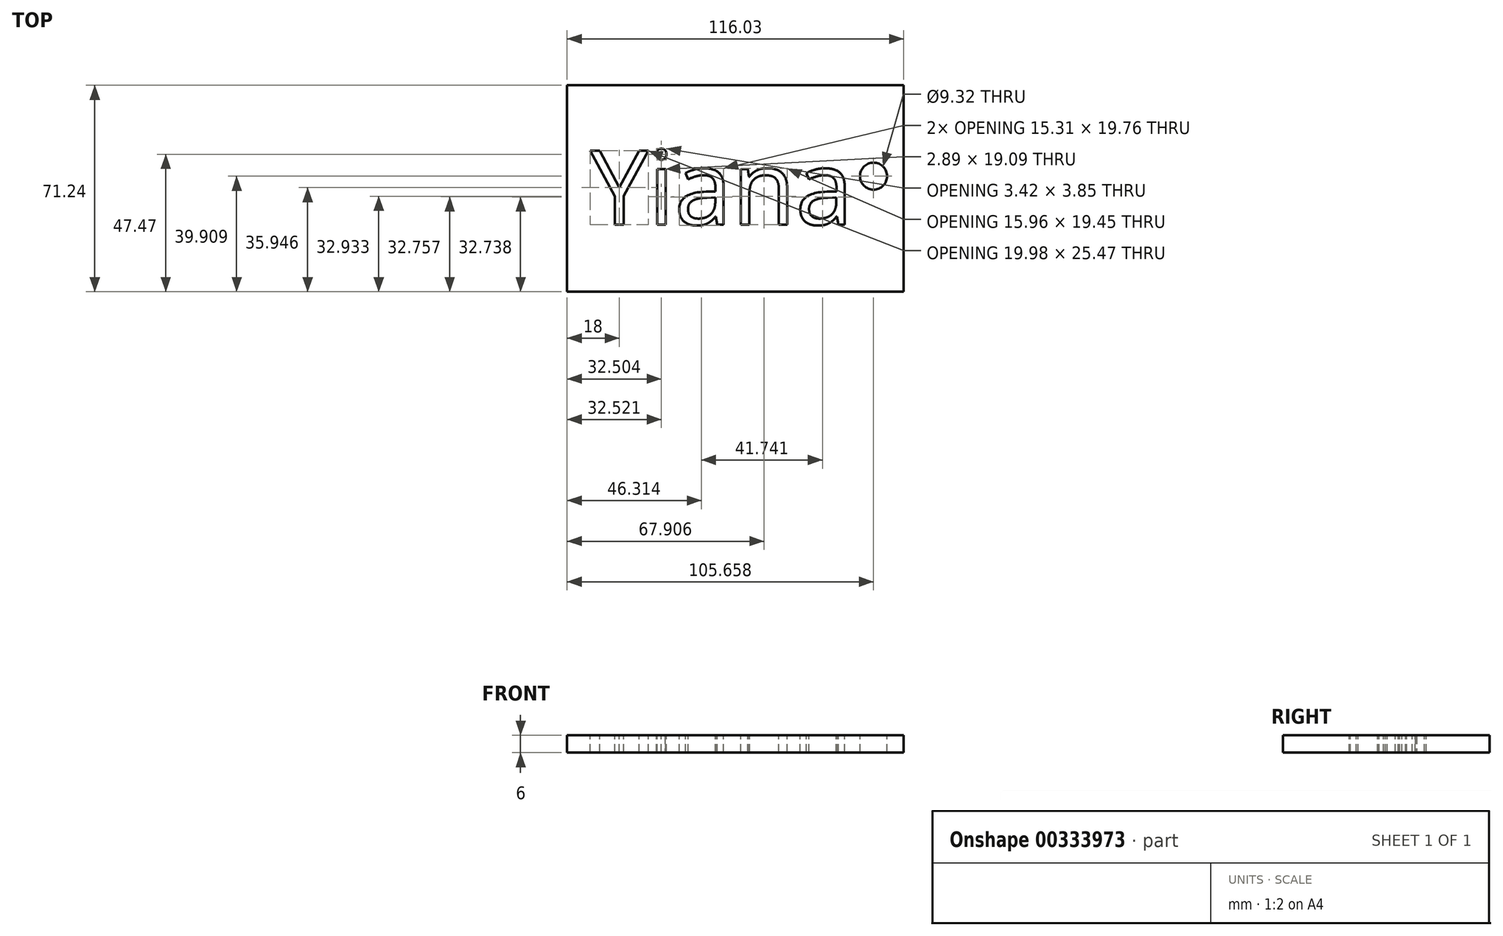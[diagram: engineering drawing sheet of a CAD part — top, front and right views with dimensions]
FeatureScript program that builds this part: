
annotation { "Feature Type Name" : "Feature", "Feature Type Description" : "" }
export const myFeature = defineFeature(function(context is Context, id is Id, definition is map)
    precondition{}
    {
        {
            var Q0;
            Q0=qCreatedBy(makeId("Top.planeOp"),FACE);
            var sketch = newSketch(context, id + "F0", { "sketchPlane" : qUnion([Q0])});
            skLineSegment(sketch, "E0.bottom", {"start": v(-77.55, 35.92) * mm, "end": v(38.48, 35.92) * mm});
            skLineSegment(sketch, "E0.top", {"start": v(-77.55, -35.32) * mm, "end": v(38.48, -35.32) * mm});
            skLineSegment(sketch, "E0.left", {"start": v(-77.55, 35.92) * mm, "end": v(-77.55, -35.32) * mm});
            skLineSegment(sketch, "E0.right", {"start": v(38.48, 35.92) * mm, "end": v(38.48, -35.32) * mm});
            skSolve(sketch);
        }
        {
            var Q0;
            Q0 = qSketchRegion(id + "F0", true);
            extrude(context, id + "F1", {"entities" : qUnion([Q0]), "depth" : 6 * mm});
        }
        {
            var Q0;
            Q0=makeQuery(id+"F1.opExtrude","CAP_FACE",FACE,{"disambiguationData":[OSD([sQuery(id+"F0.wireOp",EDGE,"E0.bottom"),sQuery(id+"F0.wireOp",EDGE,"E0.top"),sQuery(id+"F0.wireOp",EDGE,"E0.left"),sQuery(id+"F0.wireOp",EDGE,"E0.right")])],"isStart":false});
            var sketch = newSketch(context, id + "F2", { "sketchPlane" : qUnion([Q0])});
            skText(sketch, "E1", { "text": "Yiana\n", "fontName": "OpenSans-Regular.ttf"});
            skCircle(sketch, "E2", {"center": v(28.1, 4.59) * mm, "radius": 4.66 * mm});
            const initialGuessF2  = {"E1": [-0.06954, -0.01211, 1, 0, 0.02569]};
            skSetInitialGuess(sketch, initialGuessF2);
            skSolve(sketch);
        }
        {
            var Q0;
            Q0 = qSketchRegion(id + "F2", true);
            extrude(context, id + "F3", {"entities" : qUnion([Q0]), "operationType" : NewBodyOperationType.REMOVE, "oppositeDirection" : true, "depth" : 6 * mm});
        }
    });
